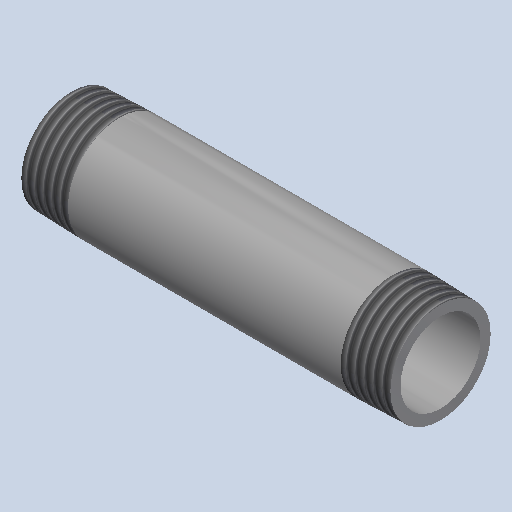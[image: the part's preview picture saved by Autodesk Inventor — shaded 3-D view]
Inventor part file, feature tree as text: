
AUTODESK INVENTOR PART (.ipt)
format: ipt  version: 2025 (Build 290162000, 162)  size: 221,696 bytes
history: native  units: mm (DEFAULTED — no unit token found)
features: other x8, revolve x1
ambient origin geometry x8: Origin, YZ Plane, XZ Plane, XY Plane, X Axis, Y Axis, Z Axis, Center Point
bodies: Solid1 (feature_tree)
feature tree (9):
  revolve  "Revolution1"  [1 undecoded]
  other  "Work Axis1"
  other  "Work Point5"
  other  "Work Axis2"
  other  "Work Point6"
  other  "Work Axis3"
  other  "Work Axis4"
  other  "Work Point7"
  other  "Work Point8"
note: 1 required parameter value undecoded (feature->parameter linkage not recoverable at this tier; creation-order binding heuristic only, values carry confidence <= 0.55)
